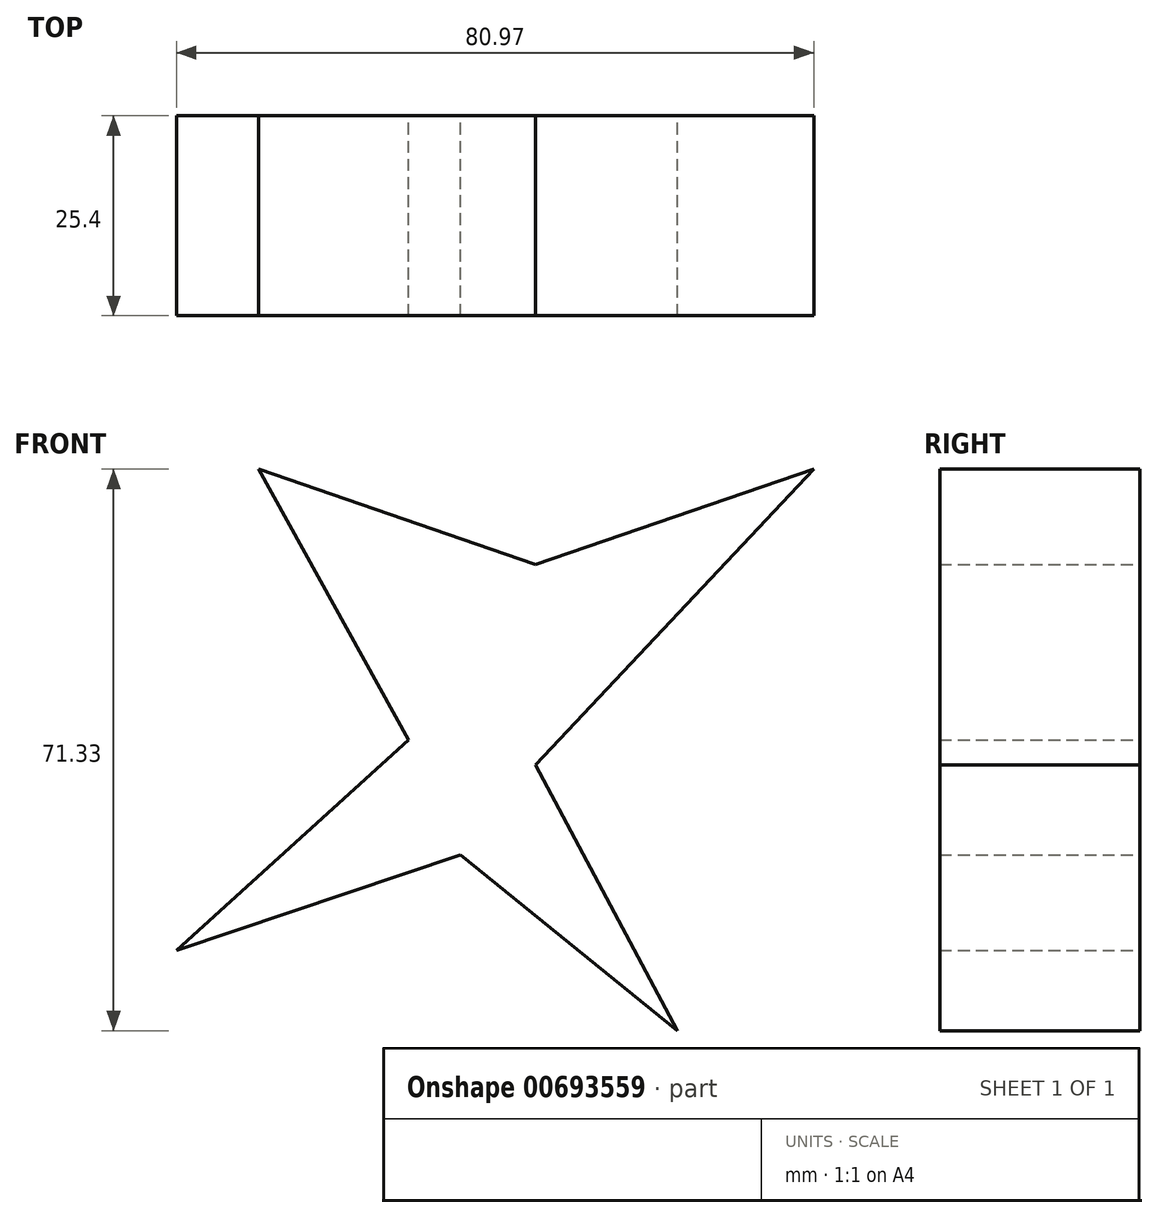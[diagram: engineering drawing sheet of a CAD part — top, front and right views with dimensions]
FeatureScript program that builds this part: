
annotation { "Feature Type Name" : "Feature", "Feature Type Description" : "" }
export const myFeature = defineFeature(function(context is Context, id is Id, definition is map)
    precondition{}
    {
        {
            var Q0;
            Q0=qCreatedBy(makeId("Front.planeOp"),FACE);
            var sketch = newSketch(context, id + "F0", { "sketchPlane" : qUnion([Q0])});
            skLineSegment(sketch, "E0", {"start": v(0, 0) * mm, "end": v(35.4, 37.6) * mm});
            skLineSegment(sketch, "E1", {"start": v(35.4, 37.6) * mm, "end": v(0, 25.48) * mm});
            skLineSegment(sketch, "E2", {"start": v(0, 25.48) * mm, "end": v(-35.12, 37.6) * mm});
            skLineSegment(sketch, "E3", {"start": v(-35.12, 37.6) * mm, "end": v(-16.11, 3.17) * mm});
            skLineSegment(sketch, "E4", {"start": v(-16.11, 3.17) * mm, "end": v(-45.58, -23.55) * mm});
            skLineSegment(sketch, "E5", {"start": v(-45.58, -23.55) * mm, "end": v(-9.5, -11.43) * mm});
            skLineSegment(sketch, "E6", {"start": v(-9.5, -11.43) * mm, "end": v(18.04, -33.74) * mm});
            skLineSegment(sketch, "E7", {"start": v(18.04, -33.74) * mm, "end": v(0, 0) * mm});
            skSolve(sketch);
        }
        {
            var Q0;
            Q0=makeQuery(id+"F0.imprint","IMPRINT",FACE,{"disambiguationData":[TD([[makeQuery(id+"F0.imprint","IMPRINT",EDGE,{"derivedFrom":sQuery(id+"F0.wireOp",EDGE,"E0")}),1.0]])]});
            extrude(context, id + "F1", {"entities" : qUnion([Q0]), "depth" : 25.4 * mm, "offsetDistance" : 25.4 * mm});
        }
    });
